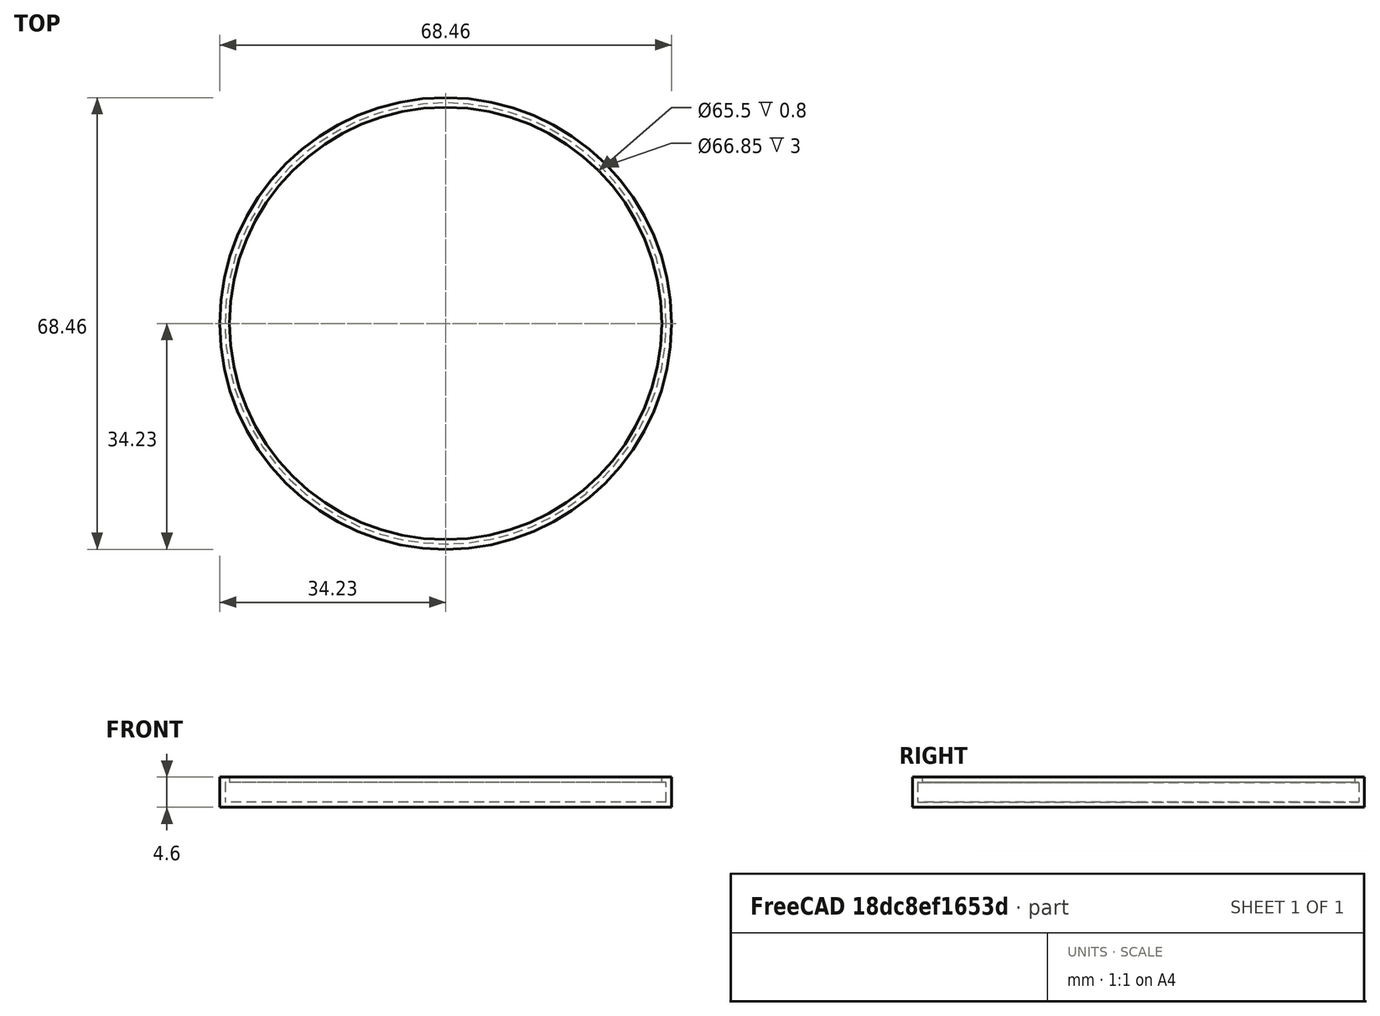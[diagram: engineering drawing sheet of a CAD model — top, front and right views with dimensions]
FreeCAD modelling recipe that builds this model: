
FCSTD DOCUMENT  (FreeCAD 0.20R29177 (Git))
Label: CatFoodLid_Moments
License: All rights reserved
LicenseURL: http://en.wikipedia.org/wiki/All_rights_reserved
objects: Sketcher::SketchObject×3, Part::Face×3, Part::Extrusion×3, Part::Fuse×2
note: 11 computed .brp shape members not serialized (recipe doc carries the construction recipe); baked Part::Feature solids carry a one-line shape summary decoded from their .brp

FEATURE [Sketcher::SketchObject] Sketch
  FullyConstrained = true
  sketch-geometry (4):
    g0: Circle CenterX=0 CenterY=0 CenterZ=0 NormalX=0 NormalY=0 NormalZ=1 AngleXU=0 Radius=33.425
    g1: Circle CenterX=0 CenterY=0 CenterZ=0 NormalX=0 NormalY=0 NormalZ=1 AngleXU=0 Radius=34.225
    g2: GeomPoint X=34.225 Y=0 Z=0
    g3: GeomPoint X=33.425 Y=0 Z=0
  constraints (8):
    c: Coincident(g0,g-1)
    c: Diameter(g0) = 66.85
    c: Coincident(g1,g0)
    c: PointOnObject(g2,g1)
    c: PointOnObject(g3,g0)
    c: PointOnObject(g3,g-1)
    c: PointOnObject(g2,g-1)
    c: Distance(g3,g2) = 0.8
FEATURE [Part::Face] Face
  FaceMakerClass = Part::FaceMakerBullseye
  Sources = -> [Sketch]
FEATURE [Part::Extrusion] Extrude
  Base = -> Sketch
  Dir = (0,0,1)
  DirMode = 2
  FaceMakerClass = Part::FaceMakerBullseye
  LengthFwd = 0.8
  LengthRev = 0
  Solid = true
  Symmetric = false
FEATURE [Sketcher::SketchObject] Sketch001
  ExternalGeometry = -> [Extrude]
  FullyConstrained = true
  MapMode = 5
  Placement = pos=(0,0,0.8) rot=(0,0,1;0rad)
  Support = -> [Extrude]
  sketch-geometry (4):
    g0: Circle CenterX=0 CenterY=0 CenterZ=0 NormalX=0 NormalY=0 NormalZ=1 AngleXU=0 Radius=34.225
    g1: GeomPoint X=34.225 Y=0 Z=0
    g2: Circle CenterX=0 CenterY=0 CenterZ=0 NormalX=0 NormalY=0 NormalZ=1 AngleXU=0 Radius=34.225
    g3: Circle CenterX=0 CenterY=0 CenterZ=0 NormalX=0 NormalY=0 NormalZ=1 AngleXU=0 Radius=33.425
  constraints (8):
    c: PointOnObject(g1,g0)
    c: PointOnObject(g1,g-1)
    c: Coincident(g2,g0)
    c: PointOnObject(g1,g2)
    c: Coincident(g0,g-1)
    c: PointOnObject(g1,g-3)
    c: Coincident(g3,g0)
    c: Diameter(g3) = 66.85
FEATURE [Part::Face] Face001
  FaceMakerClass = Part::FaceMakerBullseye
  Sources = -> [Sketch001]
FEATURE [Part::Extrusion] Extrude001
  Base = -> Sketch001
  Dir = (0,0,1)
  DirMode = 2
  FaceMakerClass = Part::FaceMakerBullseye
  LengthFwd = 3
  LengthRev = 0
  Solid = true
  Symmetric = false
FEATURE [Sketcher::SketchObject] Sketch002
  ExternalGeometry = -> [Extrude001]
  FullyConstrained = true
  MapMode = 5
  Placement = pos=(0,0,3.8) rot=(0,0,1;0rad)
  Support = -> [Extrude001]
  sketch-geometry (2):
    g0: Circle CenterX=0 CenterY=0 CenterZ=0 NormalX=0 NormalY=0 NormalZ=1 AngleXU=0 Radius=34.225
    g1: Circle CenterX=0 CenterY=0 CenterZ=0 NormalX=0 NormalY=0 NormalZ=1 AngleXU=0 Radius=32.75
  constraints (4):
    c: Coincident(g0,g-3)
    c: Equal(g0,g-3)
    c: Coincident(g1,g0)
    c: Diameter(g1) = 65.5
FEATURE [Part::Face] Face002
  FaceMakerClass = Part::FaceMakerBullseye
  Sources = -> [Sketch002]
FEATURE [Part::Extrusion] Extrude002
  Base = -> Face002
  Dir = (0,0,1)
  DirMode = 2
  FaceMakerClass = Part::FaceMakerBullseye
  LengthFwd = 0.8
  LengthRev = 0
  Solid = false
  Symmetric = false
FEATURE [Part::Fuse] Fusion
  Base = -> Extrude
  Tool = -> Extrude002
FEATURE [Part::Fuse] Fusion001
  Base = -> Extrude001
  Tool = -> Fusion
